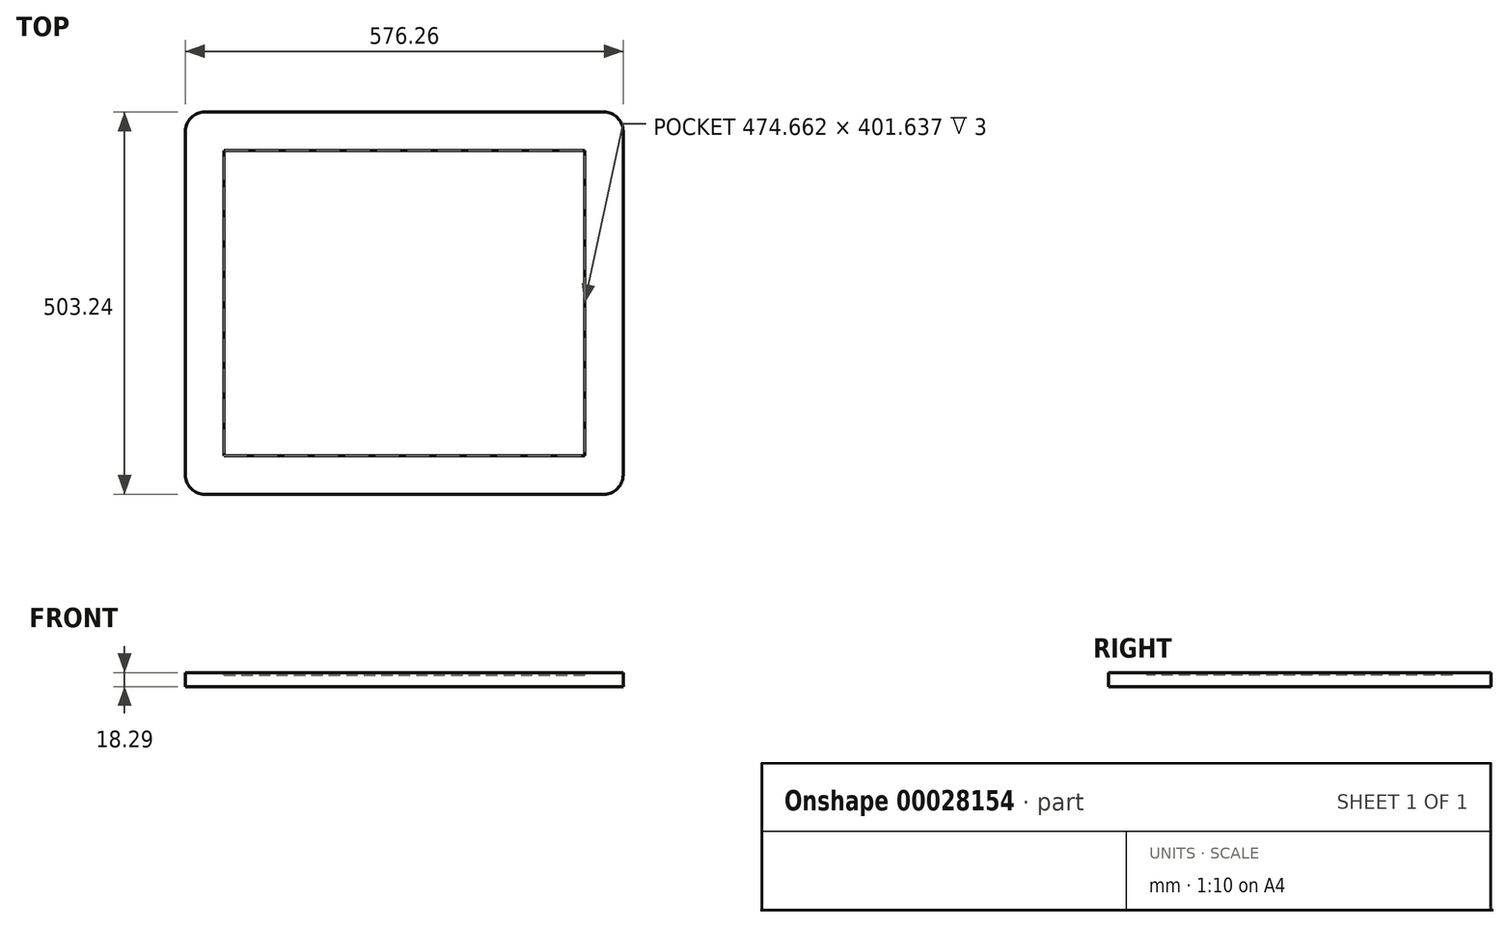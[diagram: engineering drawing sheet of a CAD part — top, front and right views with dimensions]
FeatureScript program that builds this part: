
annotation { "Feature Type Name" : "Feature", "Feature Type Description" : "" }
export const myFeature = defineFeature(function(context is Context, id is Id, definition is map)
    precondition{}
    {
        {
            var Q0;
            Q0=qCreatedBy(makeId("Top.planeOp"),FACE);
            var sketch = newSketch(context, id + "F0", { "sketchPlane" : qUnion([Q0])});
            skLineSegment(sketch, "E0.bottom", {"start": v(-356.16, 190.98) * mm, "end": v(118.5, 190.98) * mm});
            skLineSegment(sketch, "E0.top", {"start": v(-356.16, -210.66) * mm, "end": v(118.5, -210.66) * mm});
            skLineSegment(sketch, "E0.left", {"start": v(-356.16, 190.98) * mm, "end": v(-356.16, -210.66) * mm});
            skLineSegment(sketch, "E0.right", {"start": v(118.5, 190.98) * mm, "end": v(118.5, -210.66) * mm});
            skSolve(sketch);
        }
        {
            var Q0;
            Q0=makeQuery(id+"F0.imprint","IMPRINT",FACE,{"disambiguationData":[TD([[makeQuery(id+"F0.imprint","IMPRINT",EDGE,{"derivedFrom":sQuery(id+"F0.wireOp",EDGE,"E0.bottom")}),-1.0]])]});
            var sketch = newSketch(context, id + "F1", { "sketchPlane" : qUnion([Q0])});
            skLineSegment(sketch, "E1.bottom", {"start": v(-406.96, 241.78) * mm, "end": v(169.3, 241.78) * mm});
            skLineSegment(sketch, "E1.top", {"start": v(-406.96, -261.46) * mm, "end": v(169.3, -261.46) * mm});
            skLineSegment(sketch, "E1.left", {"start": v(-406.96, 241.78) * mm, "end": v(-406.96, -261.46) * mm});
            skLineSegment(sketch, "E1.right", {"start": v(169.3, 241.78) * mm, "end": v(169.3, -261.46) * mm});
            skSolve(sketch);
        }
        {
            var Q0;
            Q0=makeQuery(id+"F1.imprint","IMPRINT",FACE,{"disambiguationData":[TD([[makeQuery(id+"F1.imprint","IMPRINT",EDGE,{"derivedFrom":sQuery(id+"F1.wireOp",EDGE,"E1.bottom")}),-1.0]])]});
            var Q1;
            Q1=makeQuery(id+"F1.imprint","IMPRINT",FACE,{"disambiguationData":[TD([[makeQuery(id+"F1.imprint","IMPRINT",EDGE,{"derivedFrom":makeQuery(id+"F0.imprint","IMPRINT",EDGE,{"derivedFrom":sQuery(id+"F0.wireOp",EDGE,"E0.bottom")})}),-1.0]])]});
            extrude(context, id + "F2", {"entities" : qUnion([Q0, Q1]), "oppositeDirection" : true, "depth" : 18.29 * mm});
        }
        {
            var Q0;
            Q0 = qSketchRegion(id + "F0", true);
            extrude(context, id + "F3", {"entities" : qUnion([Q0]), "operationType" : NewBodyOperationType.REMOVE, "oppositeDirection" : true, "depth" : 3 * mm});
        }
        {
            var Q0;
            Q0=makeQuery(id+"F2.opExtrude","SWEPT_EDGE",EDGE,{"disambiguationData":[OSD([sQuery(id+"F1.wireOp",EDGE,"E1.top"),sQuery(id+"F1.wireOp",EDGE,"E1.left")])]});
            fillet(context, id + "F4", {"entities" : qUnion([Q0]), "radius" : 25.4 * mm, "tangentPropagation" : true, "allowEdgeOverflow" : false});
        }
        {
            var Q0;
            Q0=makeQuery(id+"F2.opExtrude","SWEPT_EDGE",EDGE,{"disambiguationData":[OSD([sQuery(id+"F1.wireOp",EDGE,"E1.bottom"),sQuery(id+"F1.wireOp",EDGE,"E1.left")])]});
            fillet(context, id + "F5", {"entities" : qUnion([Q0]), "radius" : 25.4 * mm, "tangentPropagation" : true, "allowEdgeOverflow" : false});
        }
        {
            var Q0;
            Q0=makeQuery(id+"F2.opExtrude","SWEPT_EDGE",EDGE,{"disambiguationData":[OSD([sQuery(id+"F1.wireOp",EDGE,"E1.top"),sQuery(id+"F1.wireOp",EDGE,"E1.right")])]});
            fillet(context, id + "F6", {"entities" : qUnion([Q0]), "radius" : 25.4 * mm, "tangentPropagation" : true, "allowEdgeOverflow" : false});
        }
        {
            var Q0;
            Q0=makeQuery(id+"F2.opExtrude","SWEPT_EDGE",EDGE,{"disambiguationData":[OSD([sQuery(id+"F1.wireOp",EDGE,"E1.bottom"),sQuery(id+"F1.wireOp",EDGE,"E1.right")])]});
            fillet(context, id + "F7", {"entities" : qUnion([Q0]), "radius" : 25.4 * mm, "tangentPropagation" : true, "allowEdgeOverflow" : false});
        }
    });
